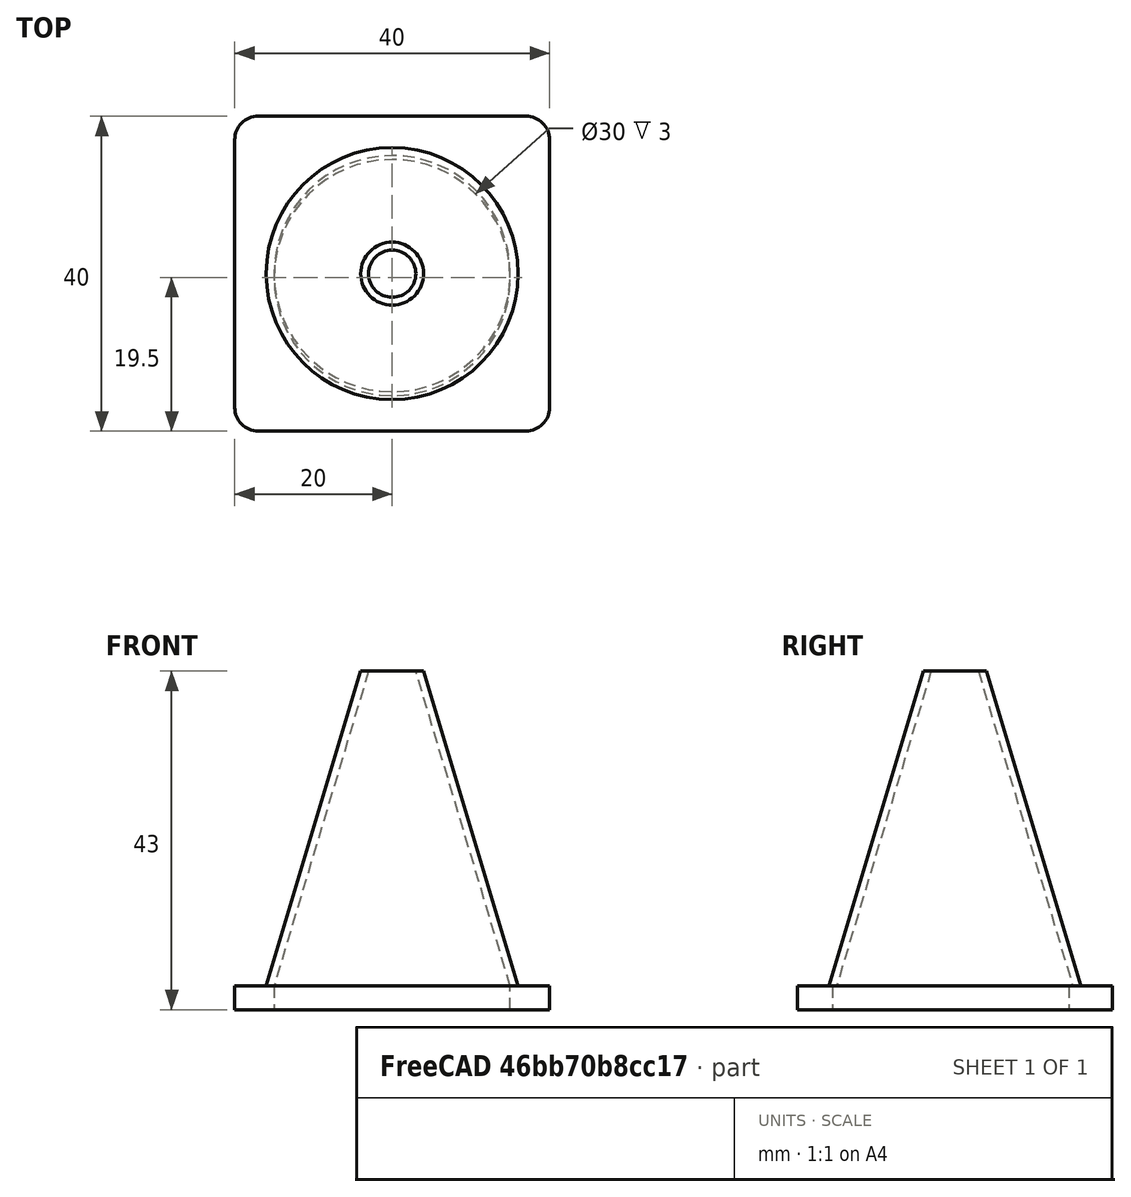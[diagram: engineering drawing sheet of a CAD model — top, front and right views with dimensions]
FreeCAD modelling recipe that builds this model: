
FCSTD DOCUMENT  (FreeCAD 0.21R33694 (Git))
Label: OJT1_T14R02_con_trafic
License: All rights reserved
LicenseURL: https://en.wikipedia.org/wiki/All_rights_reserved
objects: Part::Fillet×4, Part::Cone×2, Part::Cut×2, Part::Box×1, Part::Cylinder×1
note: 10 computed .brp shape members not serialized (recipe doc carries the construction recipe); baked Part::Feature solids carry a one-line shape summary decoded from their .brp

FEATURE [Part::Box] Box  label="Cub"
  AttacherType = Attacher::AttachEngine3D
  Height = 3
  Length = 40
  Width = 40
FEATURE [Part::Fillet] Fillet
  Base = -> Box
  Edges = 1 edges r=3: [Edge5]
FEATURE [Part::Fillet] Fillet001
  Base = -> Fillet
  Edges = 1 edges r=3: [Edge4]
FEATURE [Part::Fillet] Fillet002
  Base = -> Fillet001
  Edges = 1 edges r=3: [Edge18]
FEATURE [Part::Fillet] Fillet003
  Base = -> Fillet002
  Edges = 1 edges r=3: [Edge10]
FEATURE [Part::Cone] Cone  label="Con-exterior"
  Angle = 360
  AttacherType = Attacher::AttachEngine3D
  Height = 40
  Placement = pos=(20,20,3) rot=(0,0,1;0rad)
  Radius1 = 16
  Radius2 = 4
FEATURE [Part::Cone] Cone001  label="Con-interior"
  Angle = 360
  AttacherType = Attacher::AttachEngine3D
  Height = 40
  Placement = pos=(20,20,3) rot=(0,0,1;0rad)
  Radius1 = 15
  Radius2 = 3
FEATURE [Part::Cut] Cut
  Base = -> Cone
  Tool = -> Cone001
FEATURE [Part::Cylinder] Cylinder  label="Cilindre"
  Angle = 360
  AttacherType = Attacher::AttachEngine3D
  FirstAngle = 0
  Height = 6
  Placement = pos=(20,19.5,-2) rot=(0,0,1;0rad)
  Radius = 15
  SecondAngle = 0
FEATURE [Part::Cut] Cut001
  Base = -> Fillet003
  Tool = -> Cylinder
